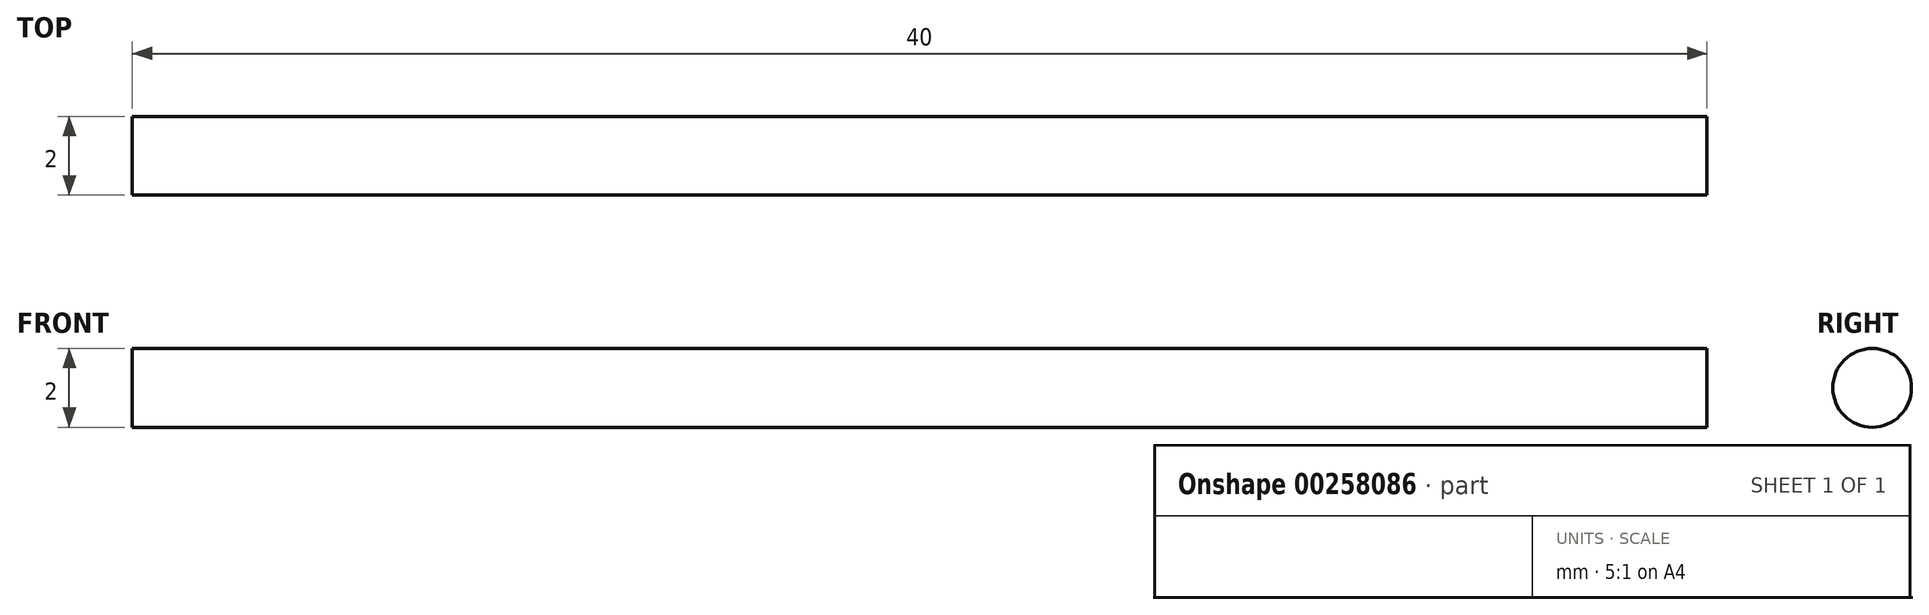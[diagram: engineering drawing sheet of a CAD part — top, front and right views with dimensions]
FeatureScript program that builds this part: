
annotation { "Feature Type Name" : "Feature", "Feature Type Description" : "" }
export const myFeature = defineFeature(function(context is Context, id is Id, definition is map)
    precondition{}
    {
        {
            var Q0;
            Q0=qCreatedBy(makeId("Top.planeOp"),FACE);
            var sketch = newSketch(context, id + "F0", { "sketchPlane" : qUnion([Q0])});
            skLineSegment(sketch, "E0", {"start": v(0, 0) * mm, "end": v(-20, 0) * mm});
            skLineSegment(sketch, "E1", {"start": v(-20, 0) * mm, "end": v(-20, 1) * mm});
            skLineSegment(sketch, "E2", {"start": v(-20, 1) * mm, "end": v(20, 1) * mm});
            skLineSegment(sketch, "E3", {"start": v(20, 1) * mm, "end": v(20, 0) * mm});
            skLineSegment(sketch, "E4", {"start": v(20, 0) * mm, "end": v(0, 0) * mm});
            skSolve(sketch);
        }
        {
            var Q0;
            Q0=makeQuery(id+"F0.imprint","IMPRINT",FACE,{"disambiguationData":[TD([[makeQuery(id+"F0.imprint","IMPRINT",EDGE,{"derivedFrom":sQuery(id+"F0.wireOp",EDGE,"E0")}),-1.0]])]});
            var Q1;
            Q1=sQuery(id+"F0.wireOp",EDGE,"E0");
            revolve(context, id + "F1", {"entities" : qUnion([Q0]), "axis" : qUnion([Q1]), "revolveType" : RevolveType.FULL});
        }
    });
